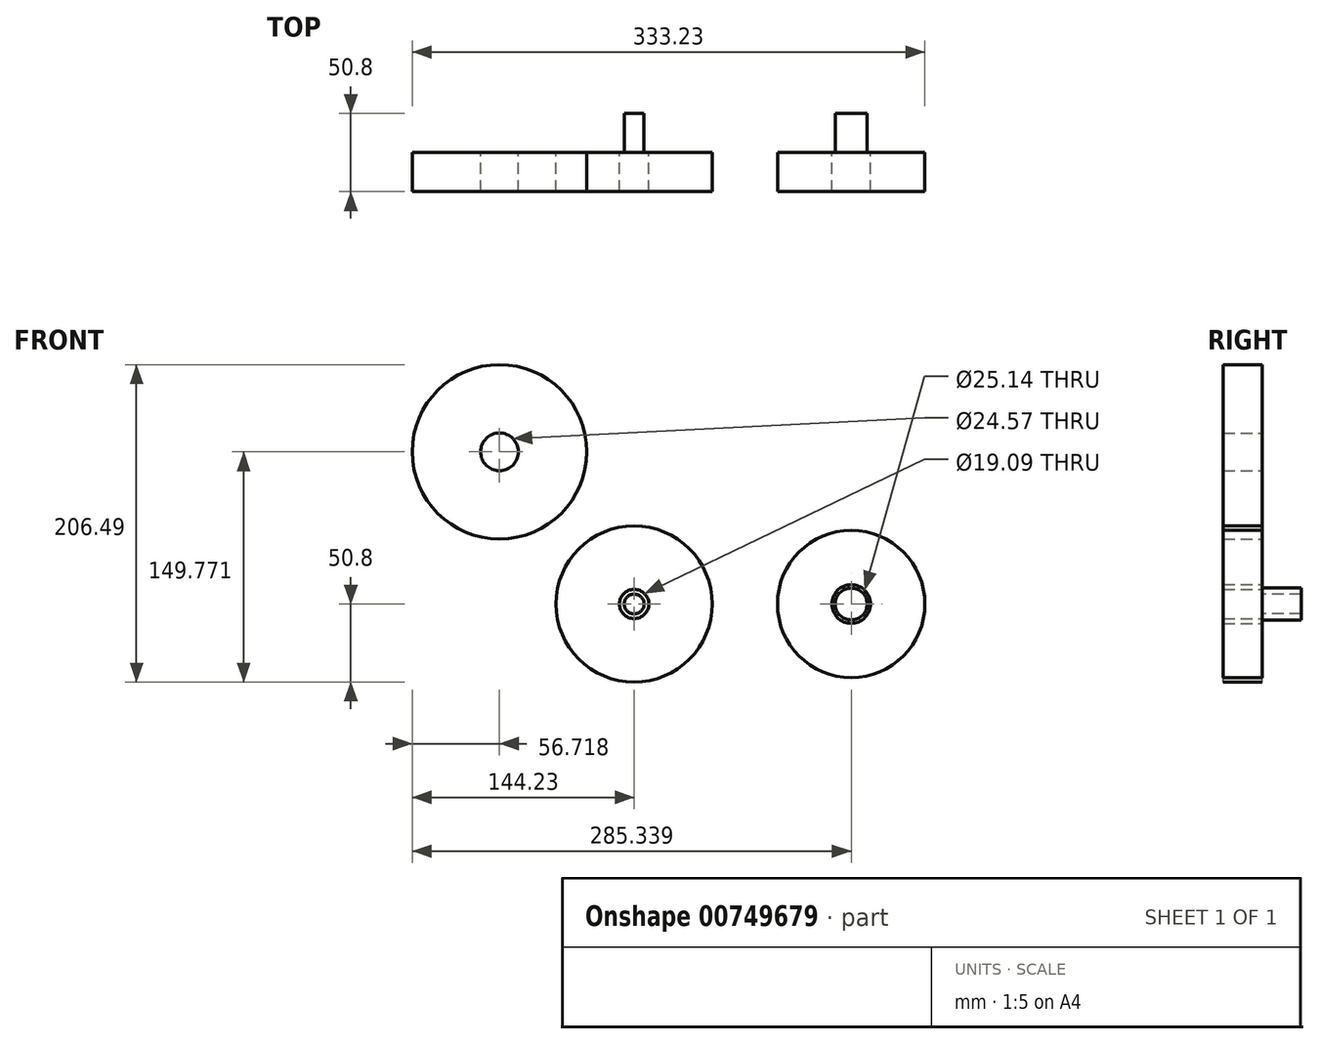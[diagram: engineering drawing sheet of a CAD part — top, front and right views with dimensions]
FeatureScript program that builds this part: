
annotation { "Feature Type Name" : "Feature", "Feature Type Description" : "" }
export const myFeature = defineFeature(function(context is Context, id is Id, definition is map)
    precondition{}
    {
        {
            var Q0;
            Q0=qCreatedBy(makeId("Front.planeOp"),FACE);
            var sketch = newSketch(context, id + "F0", { "sketchPlane" : qUnion([Q0])});
            skCircle(sketch, "E0", {"center": v(0, 0) * mm, "radius": 50.8 * mm});
            skCircle(sketch, "E1", {"center": v(0, 0) * mm, "radius": 9.55 * mm});
            skSolve(sketch);
        }
        {
            var Q0;
            Q0 = qSketchRegion(id + "F0", true);
            extrude(context, id + "F1", {"entities" : qUnion([Q0]), "depth" : 25.4 * mm, "offsetDistance" : 25.4 * mm});
        }
        {
            var Q0;
            Q0=qCreatedBy(makeId("Front.planeOp"),FACE);
            var sketch = newSketch(context, id + "F2", { "sketchPlane" : qUnion([Q0])});
            skCircle(sketch, "E2", {"center": v(-87.51, 98.97) * mm, "radius": 56.72 * mm});
            skCircle(sketch, "E3", {"center": v(-87.51, 98.97) * mm, "radius": 12.29 * mm});
            skSolve(sketch);
        }
        {
            var Q0;
            Q0=makeQuery(id+"F2.imprint","IMPRINT",FACE,{"disambiguationData":[TD([[makeQuery(id+"F2.imprint","IMPRINT",EDGE,{"derivedFrom":sQuery(id+"F2.wireOp",EDGE,"E2")}),1.0]])]});
            extrude(context, id + "F3", {"entities" : qUnion([Q0]), "depth" : 25.4 * mm, "offsetDistance" : 25.4 * mm});
        }
        {
            var Q0;
            Q0=qCreatedBy(makeId("Front.planeOp"),FACE);
            var sketch = newSketch(context, id + "F4", { "sketchPlane" : qUnion([Q0])});
            skCircle(sketch, "E4", {"center": v(141.1, 0) * mm, "radius": 47.9 * mm});
            skCircle(sketch, "E5", {"center": v(141.1, 0) * mm, "radius": 12.57 * mm});
            skSolve(sketch);
        }
        {
            var Q0;
            Q0 = qSketchRegion(id + "F4", true);
            extrude(context, id + "F5", {"entities" : qUnion([Q0]), "depth" : 25.4 * mm, "offsetDistance" : 25.4 * mm});
        }
        {
            var Q0;
            Q0=makeQuery(id+"F5.opExtrude","CAP_FACE",FACE,{"disambiguationData":[OSD([sQuery(id+"F4.wireOp",EDGE,"E4"),sQuery(id+"F4.wireOp",EDGE,"E5")])],"isStart":true});
            var sketch = newSketch(context, id + "F6", { "sketchPlane" : qUnion([Q0])});
            skCircle(sketch, "E6", {"center": v(-141.1, 0) * mm, "radius": 10.36 * mm});
            skSolve(sketch);
        }
        {
            var Q0;
            Q0 = qSketchRegion(id + "F6", true);
            extrude(context, id + "F7", {"entities" : qUnion([Q0]), "depth" : 25.4 * mm, "offsetDistance" : 25.4 * mm});
        }
        {
            var Q0;
            Q0=makeQuery(id+"F1.opExtrude","CAP_FACE",FACE,{"disambiguationData":[OSD([sQuery(id+"F0.wireOp",EDGE,"E0"),sQuery(id+"F0.wireOp",EDGE,"E1")])],"isStart":true});
            var sketch = newSketch(context, id + "F8", { "sketchPlane" : qUnion([Q0])});
            skCircle(sketch, "E7", {"center": v(0, 0) * mm, "radius": 6.47 * mm});
            skSolve(sketch);
        }
        {
            var Q0;
            Q0=makeQuery(id+"F8.imprint","IMPRINT",FACE,{"disambiguationData":[TD([[makeQuery(id+"F8.imprint","IMPRINT",EDGE,{"derivedFrom":sQuery(id+"F8.wireOp",EDGE,"E7")}),1.0]])]});
            extrude(context, id + "F9", {"entities" : qUnion([Q0]), "depth" : 25.4 * mm, "offsetDistance" : 25.4 * mm});
        }
    });
